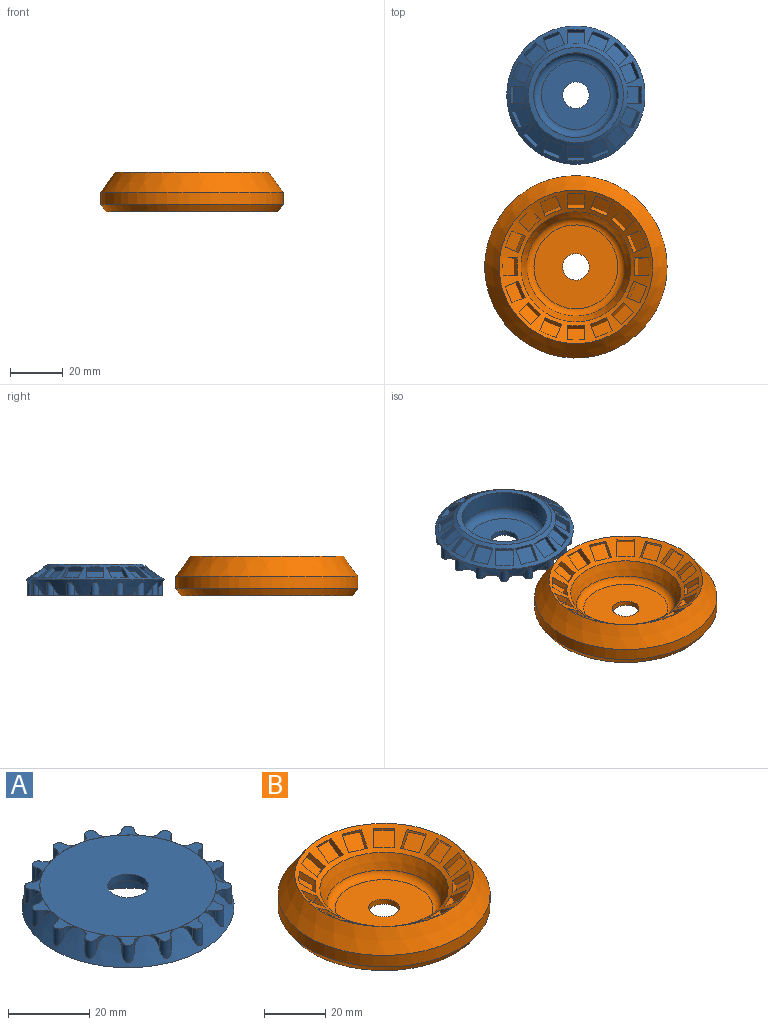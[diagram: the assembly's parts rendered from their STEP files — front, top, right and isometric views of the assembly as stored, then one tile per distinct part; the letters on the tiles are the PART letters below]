
ASSEMBLY  parts=2 mates=1
PART A: 152 faces, bbox 52.8x52.8x12.5 mm
  f0: cylinder r=1.5mm len=5.22mm, axis (0,0,1), area 21.1mm2, adj f1,f2,f3,f137
  f1: cylinder r=2.54mm len=3.16mm, axis (0,0,1), area 5.4mm2, adj f0,f3,f137
  f2: cylinder r=2.54mm len=3.16mm, axis (0,0,1), area 5.4mm2, adj f0,f3,f137
  f3: plane 6.36x5.1mm, normal (0,0,1), area 12.1mm2, adj f0,f1,f2,f137
  f4: cylinder r=1.5mm len=5.22mm, axis (0,0,1), area 21.1mm2, adj f5,f6,f7,f137
  f5: cylinder r=2.54mm len=3.16mm, axis (0,0,1), area 5.4mm2, adj f4,f7,f137
  f6: cylinder r=2.54mm len=3.16mm, axis (0,0,1), area 5.4mm2, adj f4,f7,f137
  f7: plane 5.68x5.68mm, normal (0,0,1), area 12.1mm2, adj f4,f5,f6,f137
  f8: cylinder r=1.5mm len=5.22mm, axis (0,0,1), area 21.1mm2, adj f9,f10,f11,f137
  f9: cylinder r=2.54mm len=3.16mm, axis (0,0,1), area 5.4mm2, adj f8,f11,f137
  f10: cylinder r=2.54mm len=3.16mm, axis (0,0,1), area 5.4mm2, adj f8,f11,f137
  f11: plane 6.36x5.1mm, normal (0,0,1), area 12.1mm2, adj f8,f9,f10,f137
  f12: cylinder r=1.5mm len=5.22mm, axis (0,0,1), area 21.1mm2, adj f13,f14,f15,f137
  f13: cylinder r=2.54mm len=3.16mm, axis (0,0,1), area 5.4mm2, adj f12,f15,f137
  f14: cylinder r=2.54mm len=3.16mm, axis (0,0,1), area 5.4mm2, adj f12,f15,f137
  f15: plane 6.88x3.97mm, normal (0,0,1), area 12.1mm2, adj f12,f13,f14,f137
  f16: cylinder r=1.5mm len=5.22mm, axis (0,0,1), area 21.1mm2, adj f17,f18,f19,f137
  f17: cylinder r=2.54mm len=3.16mm, axis (0,0,1), area 5.4mm2, adj f16,f19,f137
  f18: cylinder r=2.54mm len=3.16mm, axis (0,0,1), area 5.4mm2, adj f16,f19,f137
  f19: plane 6.36x5.1mm, normal (0,0,1), area 12.1mm2, adj f16,f17,f18,f137
  f20: cylinder r=1.5mm len=5.22mm, axis (0,0,1), area 21.1mm2, adj f21,f22,f23,f137
  f21: cylinder r=2.54mm len=3.16mm, axis (0,0,1), area 5.4mm2, adj f20,f23,f137
  f22: cylinder r=2.54mm len=3.16mm, axis (0,0,1), area 5.4mm2, adj f20,f23,f137
  f23: plane 5.68x5.68mm, normal (0,0,1), area 12.1mm2, adj f20,f21,f22,f137
  f24: cylinder r=1.5mm len=5.22mm, axis (0,0,1), area 21.1mm2, adj f25,f26,f27,f137
  f25: cylinder r=2.54mm len=3.16mm, axis (0,0,1), area 5.4mm2, adj f24,f27,f137
  f26: cylinder r=2.54mm len=3.16mm, axis (0,0,1), area 5.4mm2, adj f24,f27,f137
  f27: plane 6.36x5.1mm, normal (0,0,1), area 12.1mm2, adj f24,f25,f26,f137
  f28: cylinder r=1.5mm len=5.22mm, axis (0,0,1), area 19.7mm2, adj f29,f30,f31,f137
  f29: cylinder r=2.54mm len=3.16mm, axis (0,0,1), area 5.4mm2, adj f28,f31,f137
  f30: cylinder r=2.54mm len=3.16mm, axis (0,0,1), area 5.4mm2, adj f28,f31,f137
  f31: plane 6.88x3.97mm, normal (0,0,1), area 12.1mm2, adj f28,f29,f30,f137
  f32: cylinder r=1.5mm len=5.22mm, axis (0,0,1), area 21.1mm2, adj f33,f34,f35,f137
  f33: cylinder r=2.54mm len=3.16mm, axis (0,0,1), area 5.4mm2, adj f32,f35,f137
  f34: cylinder r=2.54mm len=3.16mm, axis (0,0,1), area 5.4mm2, adj f32,f35,f137
  f35: plane 6.36x5.1mm, normal (0,0,1), area 12.1mm2, adj f32,f33,f34,f137
  f36: cylinder r=1.5mm len=5.22mm, axis (0,0,1), area 21.1mm2, adj f37,f38,f39,f137
  f37: cylinder r=2.54mm len=3.16mm, axis (0,0,1), area 5.4mm2, adj f36,f39,f137
  f38: cylinder r=2.54mm len=3.16mm, axis (0,0,1), area 5.4mm2, adj f36,f39,f137
  f39: plane 5.68x5.68mm, normal (0,0,1), area 12.1mm2, adj f36,f37,f38,f137
  f40: cylinder r=1.5mm len=5.22mm, axis (0,0,1), area 21.1mm2, adj f41,f42,f43,f137
  f41: cylinder r=2.54mm len=3.16mm, axis (0,0,1), area 5.4mm2, adj f40,f43,f137
  f42: cylinder r=2.54mm len=3.16mm, axis (0,0,1), area 5.4mm2, adj f40,f43,f137
  f43: plane 6.36x5.1mm, normal (0,0,1), area 12.1mm2, adj f40,f41,f42,f137
  f44: cylinder r=1.5mm len=5.22mm, axis (0,0,1), area 21.1mm2, adj f45,f46,f47,f137
  f45: cylinder r=2.54mm len=3.16mm, axis (0,0,1), area 5.4mm2, adj f44,f47,f137
  f46: cylinder r=2.54mm len=3.16mm, axis (0,0,1), area 5.4mm2, adj f44,f47,f137
  f47: plane 6.88x3.97mm, normal (0,0,1), area 12.1mm2, adj f44,f45,f46,f137
  f48: cylinder r=1.5mm len=5.22mm, axis (0,0,1), area 21.1mm2, adj f49,f50,f51,f137
  f49: cylinder r=2.54mm len=3.16mm, axis (0,0,1), area 5.4mm2, adj f48,f51,f137
  f50: cylinder r=2.54mm len=3.16mm, axis (0,0,1), area 5.4mm2, adj f48,f51,f137
  f51: plane 6.36x5.1mm, normal (0,0,1), area 12.1mm2, adj f48,f49,f50,f137
  f52: cylinder r=1.5mm len=5.22mm, axis (0,0,1), area 21.1mm2, adj f53,f54,f55,f137
  f53: cylinder r=2.54mm len=3.16mm, axis (0,0,1), area 5.4mm2, adj f52,f55,f137
  f54: cylinder r=2.54mm len=3.16mm, axis (0,0,1), area 5.4mm2, adj f52,f55,f137
  f55: plane 5.68x5.68mm, normal (0,0,1), area 12.1mm2, adj f52,f53,f54,f137
  f56: cylinder r=1.5mm len=5.22mm, axis (0,0,1), area 21.1mm2, adj f57,f58,f59,f137
  f57: cylinder r=2.54mm len=3.16mm, axis (0,0,1), area 5.4mm2, adj f56,f59,f137
  f58: cylinder r=2.54mm len=3.16mm, axis (0,0,1), area 5.4mm2, adj f56,f59,f137
  f59: plane 6.36x5.1mm, normal (0,0,1), area 12.1mm2, adj f56,f57,f58,f137
  f60: plane 7.07x4.01mm, normal (0.75,0.31,0.58), area 13mm2, adj f62,f63,f64,f135
  f61: plane 6.97x3.93mm, normal (-0.75,-0.31,-0.58), area 13.1mm2, adj f62,f63,f64,f135
  f62: plane 8.28x7.62mm, normal (0.53,0.22,-0.82), area 44.9mm2, adj f60,f61,f63,f64
  f63: plane 6.15x5.47mm, normal (-0.38,0.92,0), area 12.4mm2, adj f60,f61,f62,f135
  f64: plane 6.15x5.47mm, normal (0.38,-0.92,0), area 12.4mm2, adj f60,f61,f62,f135
  f65: plane 5.96x5.96mm, normal (0.58,0.58,0.58), area 13mm2, adj f67,f68,f69,f135
  f66: plane 5.87x5.87mm, normal (-0.58,-0.58,-0.58), area 13.1mm2, adj f67,f68,f69,f135
  f67: plane 8.6x8.6mm, normal (0.41,0.41,-0.82), area 44.9mm2, adj f65,f66,f68,f69
  f68: plane 5.47x4.73mm, normal (-0.71,0.71,0), area 12.4mm2, adj f65,f66,f67,f135
  f69: plane 5.47x4.73mm, normal (0.71,-0.71,0), area 12.4mm2, adj f65,f66,f67,f135
  f70: plane 7.07x4.01mm, normal (0.31,0.75,0.58), area 13mm2, adj f72,f73,f74,f135
  f71: plane 6.97x3.93mm, normal (-0.31,-0.75,-0.58), area 13.1mm2, adj f72,f73,f74,f135
  f72: plane 8.28x7.62mm, normal (0.22,0.53,-0.82), area 44.9mm2, adj f70,f71,f73,f74
  f73: plane 6.15x5.47mm, normal (-0.92,0.38,0), area 12.4mm2, adj f70,f71,f72,f135
  f74: plane 6.15x5.47mm, normal (0.92,-0.38,0), area 12.4mm2, adj f70,f71,f72,f135
  f75: plane 7.17x2.1mm, normal (0,0.82,0.58), area 13mm2, adj f77,f78,f79,f135
  f76: plane 7.07x2mm, normal (0,-0.82,-0.58), area 13.1mm2, adj f77,f78,f79,f135
  f77: plane 6.7x5.47mm, normal (0,0.58,-0.82), area 44.9mm2, adj f75,f76,f78,f79
  f78: plane 6.65x5.47mm, normal (-1,0,0), area 12.4mm2, adj f75,f76,f77,f135
  f79: plane 6.65x5.47mm, normal (1,0,0), area 12.4mm2, adj f75,f76,f77,f135
  f80: plane 7.07x4.01mm, normal (-0.31,0.75,0.58), area 13mm2, adj f82,f83,f84,f135
  f81: plane 6.97x3.93mm, normal (0.31,-0.75,-0.58), area 13.1mm2, adj f82,f83,f84,f135
  f82: plane 8.28x7.62mm, normal (-0.22,0.53,-0.82), area 44.9mm2, adj f80,f81,f83,f84
  f83: plane 6.15x5.47mm, normal (-0.92,-0.38,0), area 12.4mm2, adj f80,f81,f82,f135
  f84: plane 6.15x5.47mm, normal (0.92,0.38,0), area 12.4mm2, adj f80,f81,f82,f135
  f85: plane 5.96x5.96mm, normal (-0.58,0.58,0.58), area 13mm2, adj f87,f88,f89,f135
  f86: plane 5.87x5.87mm, normal (0.58,-0.58,-0.58), area 13.1mm2, adj f87,f88,f89,f135
  f87: plane 8.6x8.6mm, normal (-0.41,0.41,-0.82), area 44.9mm2, adj f85,f86,f88,f89
  f88: plane 5.47x4.73mm, normal (-0.71,-0.71,0), area 12.4mm2, adj f85,f86,f87,f135
  f89: plane 5.47x4.73mm, normal (0.71,0.71,0), area 12.4mm2, adj f85,f86,f87,f135
  f90: plane 7.07x4.01mm, normal (-0.75,0.31,0.58), area 13mm2, adj f92,f93,f94,f135
  f91: plane 6.97x3.93mm, normal (0.75,-0.31,-0.58), area 13.1mm2, adj f92,f93,f94,f135
  f92: plane 8.28x7.62mm, normal (-0.53,0.22,-0.82), area 44.9mm2, adj f90,f91,f93,f94
  f93: plane 6.15x5.47mm, normal (-0.38,-0.92,0), area 12.4mm2, adj f90,f91,f92,f135
  f94: plane 6.15x5.47mm, normal (0.38,0.92,0), area 12.4mm2, adj f90,f91,f92,f135
  f95: plane 7.17x2.1mm, normal (-0.82,0,0.58), area 13mm2, adj f97,f98,f99,f135
  f96: plane 7.07x2mm, normal (0.82,0,-0.58), area 13.1mm2, adj f97,f98,f99,f135
  f97: plane 6.7x5.47mm, normal (-0.58,0,-0.82), area 44.9mm2, adj f95,f96,f98,f99
  f98: plane 6.65x5.47mm, normal (0,-1,0), area 12.4mm2, adj f95,f96,f97,f135
  f99: plane 6.65x5.47mm, normal (0,1,0), area 12.4mm2, adj f95,f96,f97,f135
  f100: plane 7.07x4.01mm, normal (-0.75,-0.31,0.58), area 13mm2, adj f102,f103,f104,f135
  f101: plane 6.97x3.93mm, normal (0.75,0.31,-0.58), area 13.1mm2, adj f102,f103,f104,f135
  f102: plane 8.28x7.62mm, normal (-0.53,-0.22,-0.82), area 44.9mm2, adj f100,f101,f103,f104
  f103: plane 6.15x5.47mm, normal (0.38,-0.92,0), area 12.4mm2, adj f100,f101,f102,f135
  f104: plane 6.15x5.47mm, normal (-0.38,0.92,0), area 12.4mm2, adj f100,f101,f102,f135
  f105: plane 5.96x5.96mm, normal (-0.58,-0.58,0.58), area 13mm2, adj f107,f108,f109,f135
  f106: plane 5.87x5.87mm, normal (0.58,0.58,-0.58), area 13.1mm2, adj f107,f108,f109,f135
  f107: plane 8.6x8.6mm, normal (-0.41,-0.41,-0.82), area 44.9mm2, adj f105,f106,f108,f109
  f108: plane 5.47x4.73mm, normal (0.71,-0.71,0), area 12.4mm2, adj f105,f106,f107,f135
  f109: plane 5.47x4.73mm, normal (-0.71,0.71,0), area 12.4mm2, adj f105,f106,f107,f135
  f110: plane 7.07x4.01mm, normal (-0.31,-0.75,0.58), area 13mm2, adj f112,f113,f114,f135
  f111: plane 6.97x3.93mm, normal (0.31,0.75,-0.58), area 13.1mm2, adj f112,f113,f114,f135
  f112: plane 8.28x7.62mm, normal (-0.22,-0.53,-0.82), area 44.9mm2, adj f110,f111,f113,f114
  f113: plane 6.15x5.47mm, normal (0.92,-0.38,0), area 12.4mm2, adj f110,f111,f112,f135
  f114: plane 6.15x5.47mm, normal (-0.92,0.38,0), area 12.4mm2, adj f110,f111,f112,f135
  f115: plane 7.17x2.1mm, normal (0,-0.82,0.58), area 13mm2, adj f117,f118,f119,f135
  f116: plane 7.07x2mm, normal (0,0.82,-0.58), area 13.1mm2, adj f117,f118,f119,f135
  f117: plane 6.7x5.47mm, normal (0,-0.58,-0.82), area 44.9mm2, adj f115,f116,f118,f119
  f118: plane 6.65x5.47mm, normal (1,0,0), area 12.4mm2, adj f115,f116,f117,f135
  f119: plane 6.65x5.47mm, normal (-1,0,0), area 12.4mm2, adj f115,f116,f117,f135
  f120: plane 7.07x4.01mm, normal (0.31,-0.75,0.58), area 13mm2, adj f122,f123,f124,f135
  f121: plane 6.97x3.93mm, normal (-0.31,0.75,-0.58), area 13.1mm2, adj f122,f123,f124,f135
  f122: plane 8.28x7.62mm, normal (0.22,-0.53,-0.82), area 44.9mm2, adj f120,f121,f123,f124
  f123: plane 6.15x5.47mm, normal (0.92,0.38,0), area 12.4mm2, adj f120,f121,f122,f135
  f124: plane 6.15x5.47mm, normal (-0.92,-0.38,0), area 12.4mm2, adj f120,f121,f122,f135
  f125: plane 5.96x5.96mm, normal (0.58,-0.58,0.58), area 13mm2, adj f127,f128,f129,f135
  f126: plane 5.87x5.87mm, normal (-0.58,0.58,-0.58), area 13.1mm2, adj f127,f128,f129,f135
  f127: plane 8.6x8.6mm, normal (0.41,-0.41,-0.82), area 44.9mm2, adj f125,f126,f128,f129
  f128: plane 5.47x4.73mm, normal (0.71,0.71,0), area 12.4mm2, adj f125,f126,f127,f135
  f129: plane 5.47x4.73mm, normal (-0.71,-0.71,0), area 12.4mm2, adj f125,f126,f127,f135
  f130: plane 7.07x4.01mm, normal (0.75,-0.31,0.58), area 13mm2, adj f132,f133,f134,f135
  f131: plane 6.97x3.93mm, normal (-0.75,0.31,-0.58), area 13.1mm2, adj f132,f133,f134,f135
  f132: plane 8.28x7.62mm, normal (0.53,-0.22,-0.82), area 44.9mm2, adj f130,f131,f133,f134
  f133: plane 6.15x5.47mm, normal (0.38,0.92,0), area 12.4mm2, adj f130,f131,f132,f135
  f134: plane 6.15x5.47mm, normal (-0.38,-0.92,0), area 12.4mm2, adj f130,f131,f132,f135
  f135: cone r=26.17mm half-angle=54.7deg, axis (0,0,1), area 665.2mm2, adj f60,f61,f63,f64,f65,f66,f68,f69
  f136: plane 36.02x36.02mm, normal (0,0,-1), area 213.8mm2, adj f135,f149
  f137: cone r=21.77mm half-angle=35.3deg, axis (0,0,-1), area 812mm2, adj f0,f1,f2,f3,f4,f5,f6,f7
  f138: plane 43.54x43.54mm, normal (0,0,1), area 1410.2mm2, adj f137,f150
  f139: plane 6.82x1.75mm, normal (0.82,0,0.58), area 13mm2, adj f135,f141,f142,f143
  f140: plane 6.79x1.72mm, normal (-0.82,0,-0.58), area 13.1mm2, adj f135,f141,f142,f143
  f141: plane 6.7x5.47mm, normal (0.58,0,-0.82), area 44.9mm2, adj f139,f140,f142,f143
  f142: plane 6.65x5.47mm, normal (0,-1,0), area 12.4mm2, adj f135,f139,f140,f141
  f143: plane 6.65x5.47mm, normal (0,1,0), area 12.4mm2, adj f135,f139,f140,f141
  f144: cylinder r=1.5mm len=5.22mm, axis (0,0,1), area 21.1mm2, adj f137,f145,f146,f147
  f145: cylinder r=2.54mm len=3.16mm, axis (0,0,1), area 5.4mm2, adj f137,f144,f147
  f146: cylinder r=2.54mm len=3.16mm, axis (0,0,1), area 5.4mm2, adj f137,f144,f147
  f147: plane 6.88x3.97mm, normal (0,0,1), area 12.1mm2, adj f137,f144,f145,f146
  f148: plane 26.02x26.02mm, normal (0,0,-1), area 453.4mm2, adj f150,f151
  f149: cylinder r=16.01mm len=32.02mm, axis (0,0,-1), area 704.3mm2, adj f136,f151
  f150: cylinder r=5mm len=10mm, axis (0,0,1), area 62.8mm2, adj f138,f148
  f151: torus R=13.01mm, axis (0,0,1), area 441.8mm2, adj f148,f149
PART B: 89 faces, bbox 69.4x69.4x15.5 mm
  f0: plane 7.08x4.12mm, normal (0.75,0.31,0.58), area 13.7mm2, adj f1,f3,f4,f75
  f1: plane 8.28x7.62mm, normal (-0.53,-0.22,0.82), area 44.9mm2, adj f0,f2,f3,f4
  f2: plane 6.99x4.02mm, normal (-0.75,-0.31,-0.58), area 13.7mm2, adj f1,f3,f4,f75
  f3: plane 6.28x5.68mm, normal (0.38,-0.92,0), area 14.3mm2, adj f0,f1,f2,f75
  f4: plane 6.28x5.68mm, normal (-0.38,0.92,0), area 14.3mm2, adj f0,f1,f2,f75
  f5: plane 6.03x6.03mm, normal (0.58,0.58,0.58), area 13.7mm2, adj f6,f8,f9,f75
  f6: plane 8.6x8.6mm, normal (-0.41,-0.41,0.82), area 44.9mm2, adj f5,f7,f8,f9
  f7: plane 5.93x5.93mm, normal (-0.58,-0.58,-0.58), area 13.7mm2, adj f6,f8,f9,f75
  f8: plane 5.68x4.82mm, normal (0.71,-0.71,0), area 14.3mm2, adj f5,f6,f7,f75
  f9: plane 5.68x4.82mm, normal (-0.71,0.71,0), area 14.3mm2, adj f5,f6,f7,f75
  f10: plane 7.08x4.12mm, normal (0.31,0.75,0.58), area 13.7mm2, adj f11,f13,f14,f75
  f11: plane 8.28x7.62mm, normal (-0.22,-0.53,0.82), area 44.9mm2, adj f10,f12,f13,f14
  f12: plane 6.99x4.02mm, normal (-0.31,-0.75,-0.58), area 13.7mm2, adj f11,f13,f14,f75
  f13: plane 6.28x5.68mm, normal (0.92,-0.38,0), area 14.3mm2, adj f10,f11,f12,f75
  f14: plane 6.28x5.68mm, normal (-0.92,0.38,0), area 14.3mm2, adj f10,f11,f12,f75
  f15: plane 7.11x2.16mm, normal (0,0.82,0.58), area 13.7mm2, adj f16,f18,f19,f75
  f16: plane 6.7x5.47mm, normal (0,-0.58,0.82), area 44.9mm2, adj f15,f17,f18,f19
  f17: plane 7.03x2.06mm, normal (0,-0.82,-0.58), area 13.7mm2, adj f16,f18,f19,f75
  f18: plane 6.79x5.68mm, normal (1,0,0), area 14.3mm2, adj f15,f16,f17,f75
  f19: plane 6.79x5.68mm, normal (-1,0,0), area 14.3mm2, adj f15,f16,f17,f75
  f20: plane 7.08x4.12mm, normal (-0.31,0.75,0.58), area 13.7mm2, adj f21,f23,f24,f75
  f21: plane 8.28x7.62mm, normal (0.22,-0.53,0.82), area 44.9mm2, adj f20,f22,f23,f24
  f22: plane 6.99x4.02mm, normal (0.31,-0.75,-0.58), area 13.7mm2, adj f21,f23,f24,f75
  f23: plane 6.28x5.68mm, normal (0.92,0.38,0), area 14.3mm2, adj f20,f21,f22,f75
  f24: plane 6.28x5.68mm, normal (-0.92,-0.38,0), area 14.3mm2, adj f20,f21,f22,f75
  f25: plane 6.03x6.03mm, normal (-0.58,0.58,0.58), area 13.7mm2, adj f26,f28,f29,f75
  f26: plane 8.6x8.6mm, normal (0.41,-0.41,0.82), area 44.9mm2, adj f25,f27,f28,f29
  f27: plane 5.93x5.93mm, normal (0.58,-0.58,-0.58), area 13.7mm2, adj f26,f28,f29,f75
  f28: plane 5.68x4.82mm, normal (0.71,0.71,0), area 14.3mm2, adj f25,f26,f27,f75
  f29: plane 5.68x4.82mm, normal (-0.71,-0.71,0), area 14.3mm2, adj f25,f26,f27,f75
  f30: plane 7.08x4.12mm, normal (-0.75,0.31,0.58), area 13.7mm2, adj f31,f33,f34,f75
  f31: plane 8.28x7.62mm, normal (0.53,-0.22,0.82), area 44.9mm2, adj f30,f32,f33,f34
  f32: plane 6.99x4.02mm, normal (0.75,-0.31,-0.58), area 13.7mm2, adj f31,f33,f34,f75
  f33: plane 6.28x5.68mm, normal (0.38,0.92,0), area 14.3mm2, adj f30,f31,f32,f75
  f34: plane 6.28x5.68mm, normal (-0.38,-0.92,0), area 14.3mm2, adj f30,f31,f32,f75
  f35: plane 7.11x2.16mm, normal (-0.82,0,0.58), area 13.7mm2, adj f36,f38,f39,f75
  f36: plane 6.7x5.47mm, normal (0.58,0,0.82), area 44.9mm2, adj f35,f37,f38,f39
  f37: plane 7.03x2.06mm, normal (0.82,0,-0.58), area 13.7mm2, adj f36,f38,f39,f75
  f38: plane 6.79x5.68mm, normal (0,1,0), area 14.3mm2, adj f35,f36,f37,f75
  f39: plane 6.79x5.68mm, normal (0,-1,0), area 14.3mm2, adj f35,f36,f37,f75
  f40: plane 7.08x4.12mm, normal (-0.75,-0.31,0.58), area 13.7mm2, adj f41,f43,f44,f75
  f41: plane 8.28x7.62mm, normal (0.53,0.22,0.82), area 44.9mm2, adj f40,f42,f43,f44
  f42: plane 6.99x4.02mm, normal (0.75,0.31,-0.58), area 13.7mm2, adj f41,f43,f44,f75
  f43: plane 6.28x5.68mm, normal (-0.38,0.92,0), area 14.3mm2, adj f40,f41,f42,f75
  f44: plane 6.28x5.68mm, normal (0.38,-0.92,0), area 14.3mm2, adj f40,f41,f42,f75
  f45: plane 6.03x6.03mm, normal (-0.58,-0.58,0.58), area 13.7mm2, adj f46,f48,f49,f75
  f46: plane 8.6x8.6mm, normal (0.41,0.41,0.82), area 44.9mm2, adj f45,f47,f48,f49
  f47: plane 5.93x5.93mm, normal (0.58,0.58,-0.58), area 13.7mm2, adj f46,f48,f49,f75
  f48: plane 5.68x4.82mm, normal (-0.71,0.71,0), area 14.3mm2, adj f45,f46,f47,f75
  f49: plane 5.68x4.82mm, normal (0.71,-0.71,0), area 14.3mm2, adj f45,f46,f47,f75
  f50: plane 7.08x4.12mm, normal (-0.31,-0.75,0.58), area 13.7mm2, adj f51,f53,f54,f75
  f51: plane 8.28x7.62mm, normal (0.22,0.53,0.82), area 44.9mm2, adj f50,f52,f53,f54
  f52: plane 6.99x4.02mm, normal (0.31,0.75,-0.58), area 13.7mm2, adj f51,f53,f54,f75
  f53: plane 6.28x5.68mm, normal (-0.92,0.38,0), area 14.3mm2, adj f50,f51,f52,f75
  f54: plane 6.28x5.68mm, normal (0.92,-0.38,0), area 14.3mm2, adj f50,f51,f52,f75
  f55: plane 7.11x2.16mm, normal (0,-0.82,0.58), area 13.7mm2, adj f56,f58,f59,f75
  f56: plane 6.7x5.47mm, normal (0,0.58,0.82), area 44.9mm2, adj f55,f57,f58,f59
  f57: plane 7.03x2.06mm, normal (0,0.82,-0.58), area 13.7mm2, adj f56,f58,f59,f75
  f58: plane 6.79x5.68mm, normal (-1,0,0), area 14.3mm2, adj f55,f56,f57,f75
  f59: plane 6.79x5.68mm, normal (1,0,0), area 14.3mm2, adj f55,f56,f57,f75
  f60: plane 7.08x4.12mm, normal (0.31,-0.75,0.58), area 13.7mm2, adj f61,f63,f64,f75
  f61: plane 8.28x7.62mm, normal (-0.22,0.53,0.82), area 44.9mm2, adj f60,f62,f63,f64
  f62: plane 6.99x4.02mm, normal (-0.31,0.75,-0.58), area 13.7mm2, adj f61,f63,f64,f75
  f63: plane 6.28x5.68mm, normal (-0.92,-0.38,0), area 14.3mm2, adj f60,f61,f62,f75
  f64: plane 6.28x5.68mm, normal (0.92,0.38,0), area 14.3mm2, adj f60,f61,f62,f75
  f65: plane 6.03x6.03mm, normal (0.58,-0.58,0.58), area 13.7mm2, adj f66,f68,f69,f75
  f66: plane 8.6x8.6mm, normal (-0.41,0.41,0.82), area 44.9mm2, adj f65,f67,f68,f69
  f67: plane 5.93x5.93mm, normal (-0.58,0.58,-0.58), area 13.7mm2, adj f66,f68,f69,f75
  f68: plane 5.68x4.82mm, normal (-0.71,-0.71,0), area 14.3mm2, adj f65,f66,f67,f75
  f69: plane 5.68x4.82mm, normal (0.71,0.71,0), area 14.3mm2, adj f65,f66,f67,f75
  f70: plane 7.08x4.12mm, normal (0.75,-0.31,0.58), area 13.7mm2, adj f71,f73,f74,f75
  f71: plane 8.28x7.62mm, normal (-0.53,0.22,0.82), area 44.9mm2, adj f70,f72,f73,f74
  f72: plane 6.99x4.02mm, normal (-0.75,0.31,-0.58), area 13.7mm2, adj f71,f73,f74,f75
  f73: plane 6.28x5.68mm, normal (-0.38,-0.92,0), area 14.3mm2, adj f70,f71,f72,f75
  f74: plane 6.28x5.68mm, normal (0.38,0.92,0), area 14.3mm2, adj f70,f71,f72,f75
  f75: cone r=29.06mm half-angle=54.7deg, axis (0,0,1), area 847.7mm2, adj f0,f2,f3,f4,f5,f7,f8,f9
  f76: cone r=20.9mm half-angle=22.2deg, axis (0,0,1), area 736.5mm2, adj f75,f88
  f77: plane 31.77x31.77mm, normal (0,0,1), area 714.2mm2, adj f78,f88
  f78: cylinder r=5mm len=10mm, axis (0,0,1), area 62.8mm2, adj f77,f79
  f79: plane 64.99x64.99mm, normal (0,0,-1), area 3239mm2, adj f78,f80
  f80: cone r=32.5mm half-angle=35deg, axis (0,0,1), area 735.2mm2, adj f79,f81
  f81: cylinder r=34.5mm len=69mm, axis (0,0,1), area 995.1mm2, adj f80,f82
  f82: cone r=34.5mm half-angle=35.3deg, axis (0,0,-1), area 1878.9mm2, adj f75,f81
  f83: plane 6.8x1.85mm, normal (0.82,0,0.58), area 13.7mm2, adj f75,f85,f86,f87
  f84: plane 6.78x1.81mm, normal (-0.82,0,-0.58), area 13.7mm2, adj f75,f85,f86,f87
  f85: plane 6.79x5.68mm, normal (0,1,0), area 14.3mm2, adj f75,f83,f84,f87
  f86: plane 6.79x5.68mm, normal (0,-1,0), area 14.3mm2, adj f75,f83,f84,f87
  f87: plane 6.7x5.47mm, normal (-0.58,0,0.82), area 44.9mm2, adj f83,f84,f85,f86
  f88: torus R=15.89mm, axis (0,0,-1), area 389.5mm2, adj f76,f77
PLACE A rot(axis=(0,-1,0),180deg) t=(0,65,25.43)mm
PLACE B at identity
MATE fastened A.f150 <-> B.f79  axis (0,0,-1) through (0,65,0)mm
